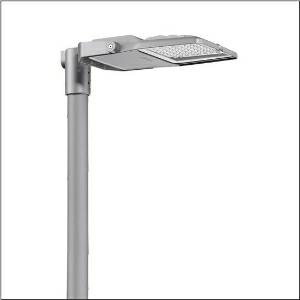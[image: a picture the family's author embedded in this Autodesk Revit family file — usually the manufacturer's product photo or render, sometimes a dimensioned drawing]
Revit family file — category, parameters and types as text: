
# Revit family: floodlight_fl_21_mini___pl33t_5xa7776c2f3a_ca81
name_source: partatom
category: Lighting Fixtures
units: mm (PartAtom-declared; Revit-internal decimal feet)

## family parameters
Cut with Voids When Loaded = No
Host = Face
Light Source = No
Part Type = Normal
Room Calculation Point = No
Round Connector Dimension = Use Diameter
Shared = No

## types (1)
- --- (1 x LED, 12050 lm, 89 W, 3000K)
    Apparent Load = 89 VA
    CIE Flux Codes = 26 75 99 100 100
    Color Rendering = 70
    Color Temperature = 3000K
    Default Elevation = 1800 mm
    Description = Floodlight FL 21 mini, floodlight, primary light control with lens, of PMMA, primary optical cover: protective disc, of toughened safety glass, transparent, light distribution: PL33T, light emission: direct distribution, installation type: surface-mounted, LED, High Power LED, rated luminous flux: 12.050lm, luminous efficacy: 135lm/W, light colour: 730, colour temperature: 3000K, control gear: ECG Smart Interface, control: flexible luminous flux parameterisation, time-dependent luminous flux control, constant luminous flux control, overheat protection, presetting dimming logarithmic, with terminal, 6-pole, mains connection: 220..240V, AC, 50/60Hz, start of lifetime: 89W, end of lifetime: 94W, reduction: 43W, luminaire housing, of diecast aluminium, powder-coated, Siteco® metallic grey (DB 702S), corrosivity category C5 according to DIN EN ISO 12944, mast bracket, of steel, galvanised, powder-coated, Siteco® metallic grey (DB 702S), protection rating (complete): IP66, insulation class (complete): insulation class II (safety insulation), certification: CE, protection symbol: D, impact resistance: IK08, permissible operating ambient temperature: -40..+40°C, permissible operating ambient temperature for outdoor applications: -40..+50°C, standard: DIN EN 12944, packaging unit: 1 piece

Light Distribution: PL33T
    Height = 70 mm
    Lamp = 1 x LED
    Lamp Light Flux = 12050 lm
    Lamp Power = 89 W
    Lamp count = 1
    Length = 485 mm
    Luminous efficacy = 135 lm/W
    Manufacturer = Siteco
    ModVariant = No
    Model = 5XA7776C2F3A
    Number of Poles = 1
    OnlyDefault = Yes
    Power Factor = 1
    Product Name = Floodlight FL 21 mini | PL33T
    Product group = floodlight | pylon top
    ProductGroupID = 6101
    Protection Class = Protection class II
    Protection Degree = IP 66
    RLX_Detail_Level = 1
    RlxData = <blob elided: 100597 chars, md5=87e9c819>
    Socket = socket
    Standby Power = 0 W
    System Light Flux = 12050 lm
    System Power = 89 W
    Type Comments = factory setting: luminous flux: 100 % | dim-lin: 254 | 456 mA
    Type Image = l_1007125.jpg
    URL = http://relux.com
    VarID = @adj_058567
    Voltage = 0 V
    Weight = 0.00 kg
    Width = 337 mm

## geometry (parser evidence)
native form markers: Blend x4, Sweep x14
no freeform markers — native parametric forms only
